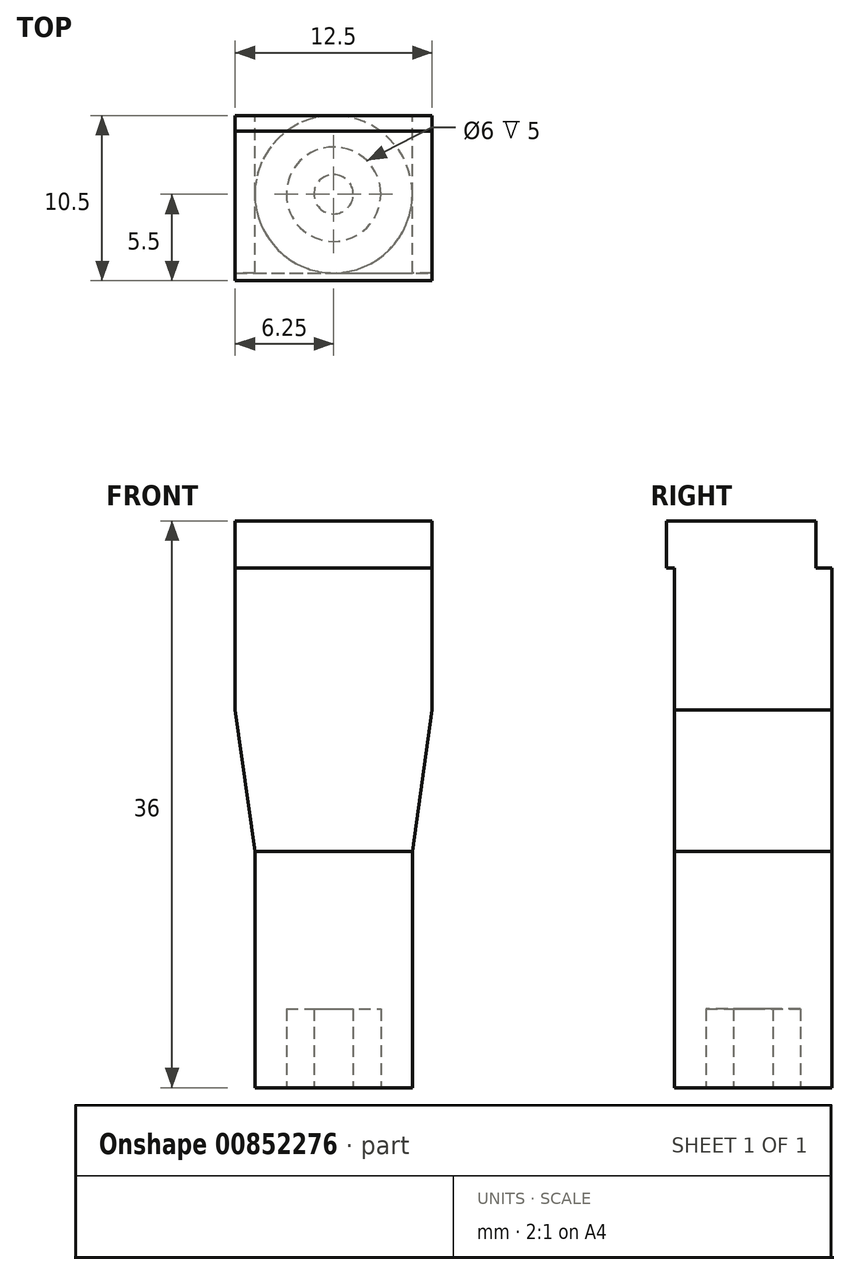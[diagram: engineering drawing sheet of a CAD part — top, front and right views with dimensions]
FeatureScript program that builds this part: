
annotation { "Feature Type Name" : "Feature", "Feature Type Description" : "" }
export const myFeature = defineFeature(function(context is Context, id is Id, definition is map)
    precondition{}
    {
        {
            var Q0;
            Q0=qCreatedBy(makeId("Front.planeOp"),FACE);
            var sketch = newSketch(context, id + "F0", { "sketchPlane" : qUnion([Q0])});
            skLineSegment(sketch, "E0", {"start": v(0, 0) * mm, "end": v(0, 15) * mm});
            skLineSegment(sketch, "E1", {"start": v(5, 15) * mm, "end": v(5, 0) * mm});
            skLineSegment(sketch, "E2", {"start": v(5, 0) * mm, "end": v(0, 0) * mm});
            skLineSegment(sketch, "E3", {"start": v(0, 15) * mm, "end": v(5, 15) * mm});
            skSolve(sketch);
        }
        {
            var Q0;
            Q0 = qSketchRegion(id + "F0", true);
            var Q1;
            Q1=sQuery(id+"F0.wireOp",EDGE,"E0");
            revolve(context, id + "F1", {"surfaceOperationType" : NewSurfaceOperationType.NEW, "entities" : qUnion([Q0]), "axis" : qUnion([Q1]), "revolveType" : RevolveType.FULL});
        }
        {
            var Q0;
            Q0=makeQuery(id+"F1.opRevolve","SWEPT_FACE",FACE,{"disambiguationData":[OSD([sQuery(id+"F0.wireOp",EDGE,"E2")])]});
            var sketch = newSketch(context, id + "F2", { "sketchPlane" : qUnion([Q0])});
            skCircle(sketch, "E4", {"center": v(0, 0) * mm, "radius": 1.25 * mm});
            skCircle(sketch, "E5", {"center": v(0, 0) * mm, "radius": 3 * mm});
            skSolve(sketch);
        }
        {
            var Q0;
            Q0 = qSketchRegion(id + "F2", true);
            extrude(context, id + "F3", {"entities" : qUnion([Q0]), "operationType" : NewBodyOperationType.REMOVE, "oppositeDirection" : true, "depth" : 5 * mm, "offsetDistance" : 25 * mm});
        }
        {
            var Q0;
            Q0=qCreatedBy(makeId("Front.planeOp"),FACE);
            var sketch = newSketch(context, id + "F4", { "sketchPlane" : qUnion([Q0])});
            skLineSegment(sketch, "E6", {"start": v(0, 0) * mm, "end": v(0, 15) * mm, "construction": true});
            skLineSegment(sketch, "E7", {"start": v(-5, 15) * mm, "end": v(5, 15) * mm});
            skLineSegment(sketch, "E8", {"start": v(0, 15) * mm, "end": v(0, 24) * mm, "construction": true});
            skLineSegment(sketch, "E9", {"start": v(-5, 15) * mm, "end": v(-6.25, 24) * mm});
            skLineSegment(sketch, "E10", {"start": v(-6.25, 24) * mm, "end": v(6.25, 24) * mm});
            skLineSegment(sketch, "E11", {"start": v(6.25, 24) * mm, "end": v(5, 15) * mm});
            skSolve(sketch);
        }
        {
            var Q0;
            Q0 = qSketchRegion(id + "F4", true);
            extrude(context, id + "F5", {"entities" : qUnion([Q0]), "operationType" : NewBodyOperationType.ADD, "endBound" : BoundingType.SYMMETRIC, "depth" : 10 * mm, "offsetDistance" : 25 * mm});
        }
        {
            var Q0;
            Q0=makeQuery(id+"F5.opExtrude","SWEPT_FACE",FACE,{"disambiguationData":[OSD([sQuery(id+"F4.wireOp",EDGE,"E10")])]});
            var sketch = newSketch(context, id + "F6", { "sketchPlane" : qUnion([Q0])});
            skLineSegment(sketch, "E12.bottom", {"start": v(-6.25, -5) * mm, "end": v(6.25, -5) * mm});
            skLineSegment(sketch, "E12.top", {"start": v(-6.25, 5) * mm, "end": v(6.25, 5) * mm});
            skLineSegment(sketch, "E12.left", {"start": v(-6.25, -5) * mm, "end": v(-6.25, 5) * mm});
            skLineSegment(sketch, "E12.right", {"start": v(6.25, -5) * mm, "end": v(6.25, 5) * mm});
            skSolve(sketch);
        }
        {
            var Q0;
            Q0 = qSketchRegion(id + "F6", true);
            extrude(context, id + "F7", {"entities" : qUnion([Q0]), "operationType" : NewBodyOperationType.ADD, "depth" : 9 * mm, "offsetDistance" : 25 * mm});
        }
        {
            var Q0;
            Q0=makeQuery(id+"F7.opExtrude","CAP_FACE",FACE,{"disambiguationData":[OSD([sQuery(id+"F6.wireOp",EDGE,"E12.bottom"),sQuery(id+"F6.wireOp",EDGE,"E12.top"),sQuery(id+"F6.wireOp",EDGE,"E12.left"),sQuery(id+"F6.wireOp",EDGE,"E12.right")])],"isStart":false});
            var sketch = newSketch(context, id + "F8", { "sketchPlane" : qUnion([Q0])});
            skLineSegment(sketch, "E13.bottom", {"start": v(-6.25, -5.5) * mm, "end": v(6.25, -5.5) * mm});
            skLineSegment(sketch, "E13.top", {"start": v(-6.25, 4) * mm, "end": v(6.25, 4) * mm});
            skLineSegment(sketch, "E13.left", {"start": v(-6.25, -5.5) * mm, "end": v(-6.25, 4) * mm});
            skLineSegment(sketch, "E13.right", {"start": v(6.25, -5.5) * mm, "end": v(6.25, 4) * mm});
            skSolve(sketch);
        }
        {
            var Q0;
            Q0 = qSketchRegion(id + "F8", true);
            extrude(context, id + "F9", {"entities" : qUnion([Q0]), "operationType" : NewBodyOperationType.ADD, "depth" : 3 * mm, "offsetDistance" : 25 * mm});
        }
    });
